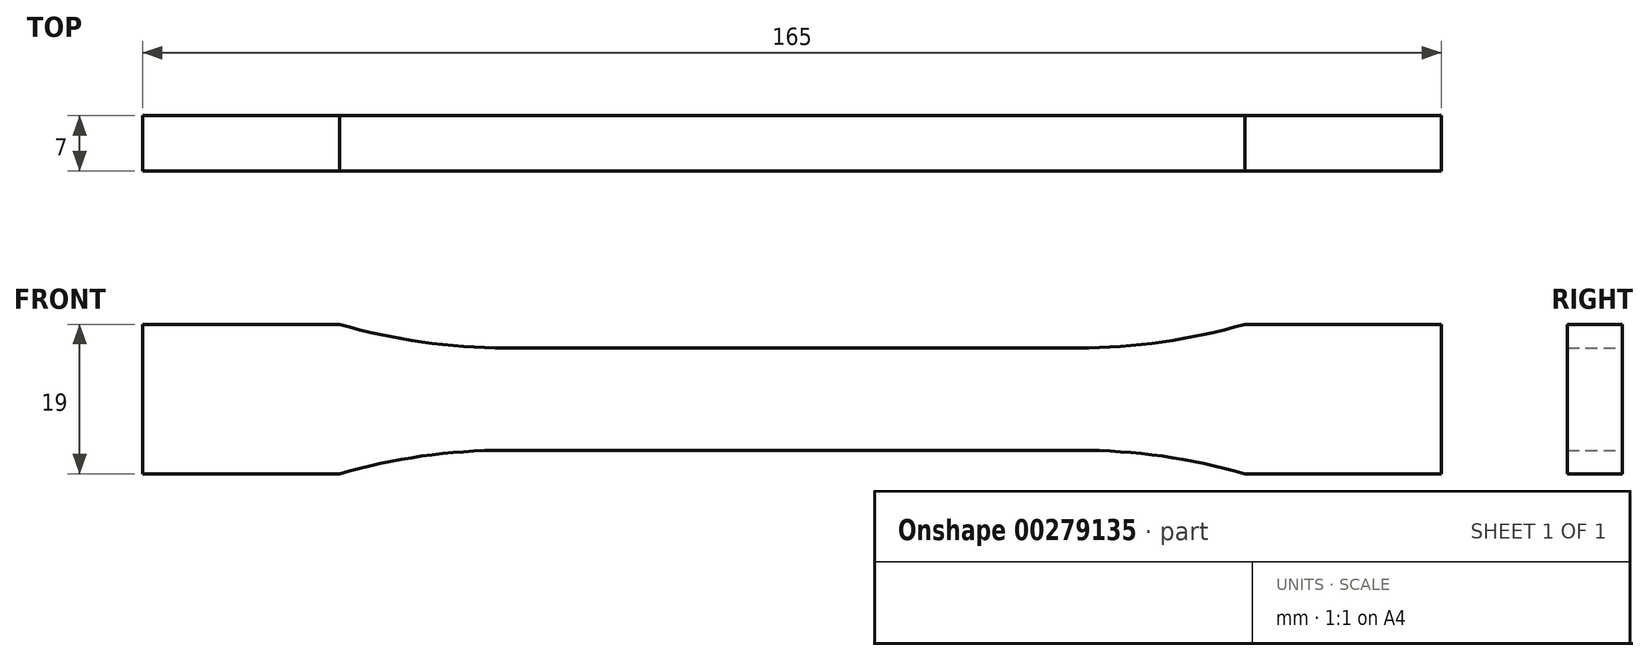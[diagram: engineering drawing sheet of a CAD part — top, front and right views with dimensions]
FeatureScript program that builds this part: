
annotation { "Feature Type Name" : "Feature", "Feature Type Description" : "" }
export const myFeature = defineFeature(function(context is Context, id is Id, definition is map)
    precondition{}
    {
        {
            var Q0;
            Q0=qCreatedBy(makeId("Front.planeOp"),FACE);
            var sketch = newSketch(context, id + "F0", { "sketchPlane" : qUnion([Q0])});
            skLineSegment(sketch, "E0", {"start": v(0, 6.5) * mm, "end": v(36.36, 6.5) * mm});
            skArc(sketch, "E1", {"start": v(36.36, 6.5) * mm, "mid": v(47.03, 7.25) * mm, "end": v(57.5, 9.5) * mm});
            skLineSegment(sketch, "E2", {"start": v(57.5, 9.5) * mm, "end": v(82.5, 9.5) * mm});
            skLineSegment(sketch, "E3.MirrorCS", {"start": v(57.5, -9.5) * mm, "end": v(82.5, -9.5) * mm});
            skLineSegment(sketch, "E4.MirrorCS", {"start": v(0, -6.5) * mm, "end": v(36.36, -6.5) * mm});
            skArc(sketch, "E5.MirrorCS", {"start": v(36.36, -6.5) * mm, "mid": v(47.03, -7.25) * mm, "end": v(57.5, -9.5) * mm});
            skLineSegment(sketch, "E6.MirrorCS", {"start": v(0, -6.5) * mm, "end": v(-36.36, -6.5) * mm});
            skLineSegment(sketch, "E7.MirrorCS", {"start": v(0, 6.5) * mm, "end": v(-36.36, 6.5) * mm});
            skArc(sketch, "E8.MirrorCS", {"start": v(-36.36, -6.5) * mm, "mid": v(-47.03, -7.25) * mm, "end": v(-57.5, -9.5) * mm});
            skArc(sketch, "E9.MirrorCS", {"start": v(-36.36, 6.5) * mm, "mid": v(-47.03, 7.25) * mm, "end": v(-57.5, 9.5) * mm});
            skLineSegment(sketch, "E10.MirrorCS", {"start": v(-57.5, 9.5) * mm, "end": v(-82.5, 9.5) * mm});
            skLineSegment(sketch, "E11.MirrorCS", {"start": v(-57.5, -9.5) * mm, "end": v(-82.5, -9.5) * mm});
            skLineSegment(sketch, "E12", {"start": v(-82.5, 9.5) * mm, "end": v(-82.5, -9.5) * mm});
            skLineSegment(sketch, "E13", {"start": v(82.5, 9.5) * mm, "end": v(82.5, -9.5) * mm});
            skSolve(sketch);
        }
        {
            var Q0;
            Q0 = qSketchRegion(id + "F0", true);
            extrude(context, id + "F1", {"entities" : qUnion([Q0]), "endBound" : BoundingType.SYMMETRIC, "depth" : 7 * mm});
        }
    });
